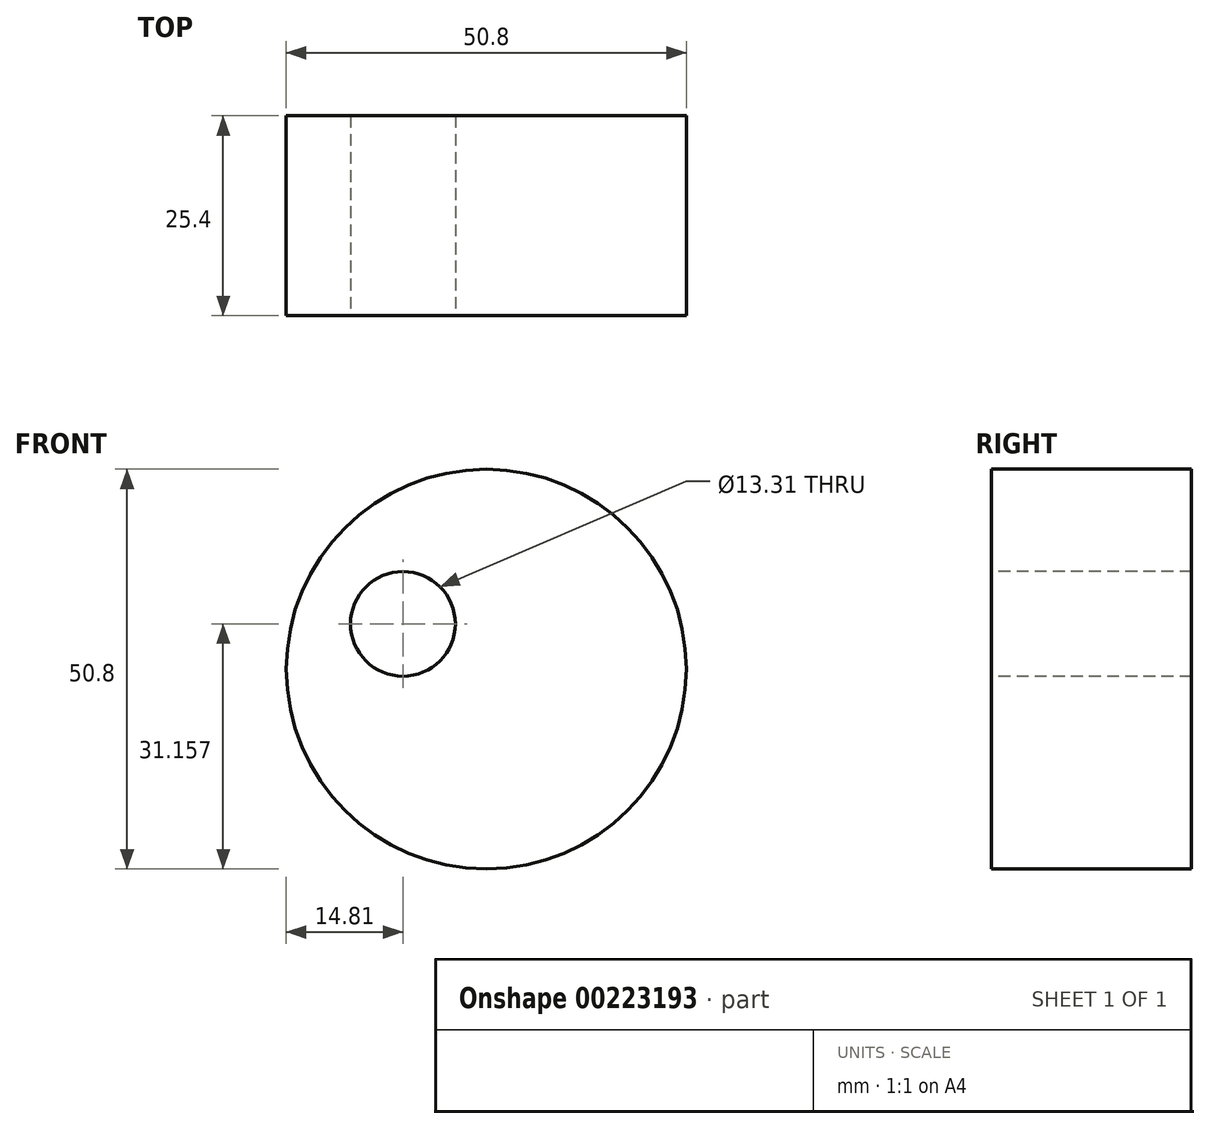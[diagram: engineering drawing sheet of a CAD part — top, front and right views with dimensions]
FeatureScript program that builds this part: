
annotation { "Feature Type Name" : "Feature", "Feature Type Description" : "" }
export const myFeature = defineFeature(function(context is Context, id is Id, definition is map)
    precondition{}
    {
        {
            var Q0;
            Q0=qCreatedBy(makeId("Front.planeOp"),FACE);
            var sketch = newSketch(context, id + "F0", { "sketchPlane" : qUnion([Q0])});
            skCircle(sketch, "E0", {"center": v(0, 0) * mm, "radius": 25.4 * mm});
            skSolve(sketch);
        }
        {
            var Q0;
            Q0=makeQuery(id+"F0.imprint","IMPRINT",FACE,{"disambiguationData":[TD([[makeQuery(id+"F0.imprint","IMPRINT",EDGE,{"derivedFrom":sQuery(id+"F0.wireOp",EDGE,"E0")}),1.0]])]});
            extrude(context, id + "F1", {"entities" : qUnion([Q0]), "depth" : 25.4 * mm});
        }
        {
            var Q0;
            Q0=makeQuery(id+"F1.opExtrude","CAP_FACE",FACE,{"disambiguationData":[OSD([sQuery(id+"F0.wireOp",EDGE,"E0")])],"isStart":false});
            var sketch = newSketch(context, id + "F2", { "sketchPlane" : qUnion([Q0])});
            skCircle(sketch, "E1", {"center": v(-10.6, 5.76) * mm, "radius": 6.65 * mm});
            skSolve(sketch);
        }
        {
            var Q0;
            Q0 = qSketchRegion(id + "F2", true);
            var Q1;
            Q1=makeQuery(id+"F1.opExtrude","CAP_FACE",FACE,{"disambiguationData":[OSD([sQuery(id+"F0.wireOp",EDGE,"E0")])],"isStart":true});
            extrude(context, id + "F3", {"entities" : qUnion([Q0]), "operationType" : NewBodyOperationType.REMOVE, "endBound" : BoundingType.UP_TO_SURFACE, "oppositeDirection" : true, "endBoundEntityFace" : qUnion([Q1]), "depth" : 25.4 * mm});
        }
    });
